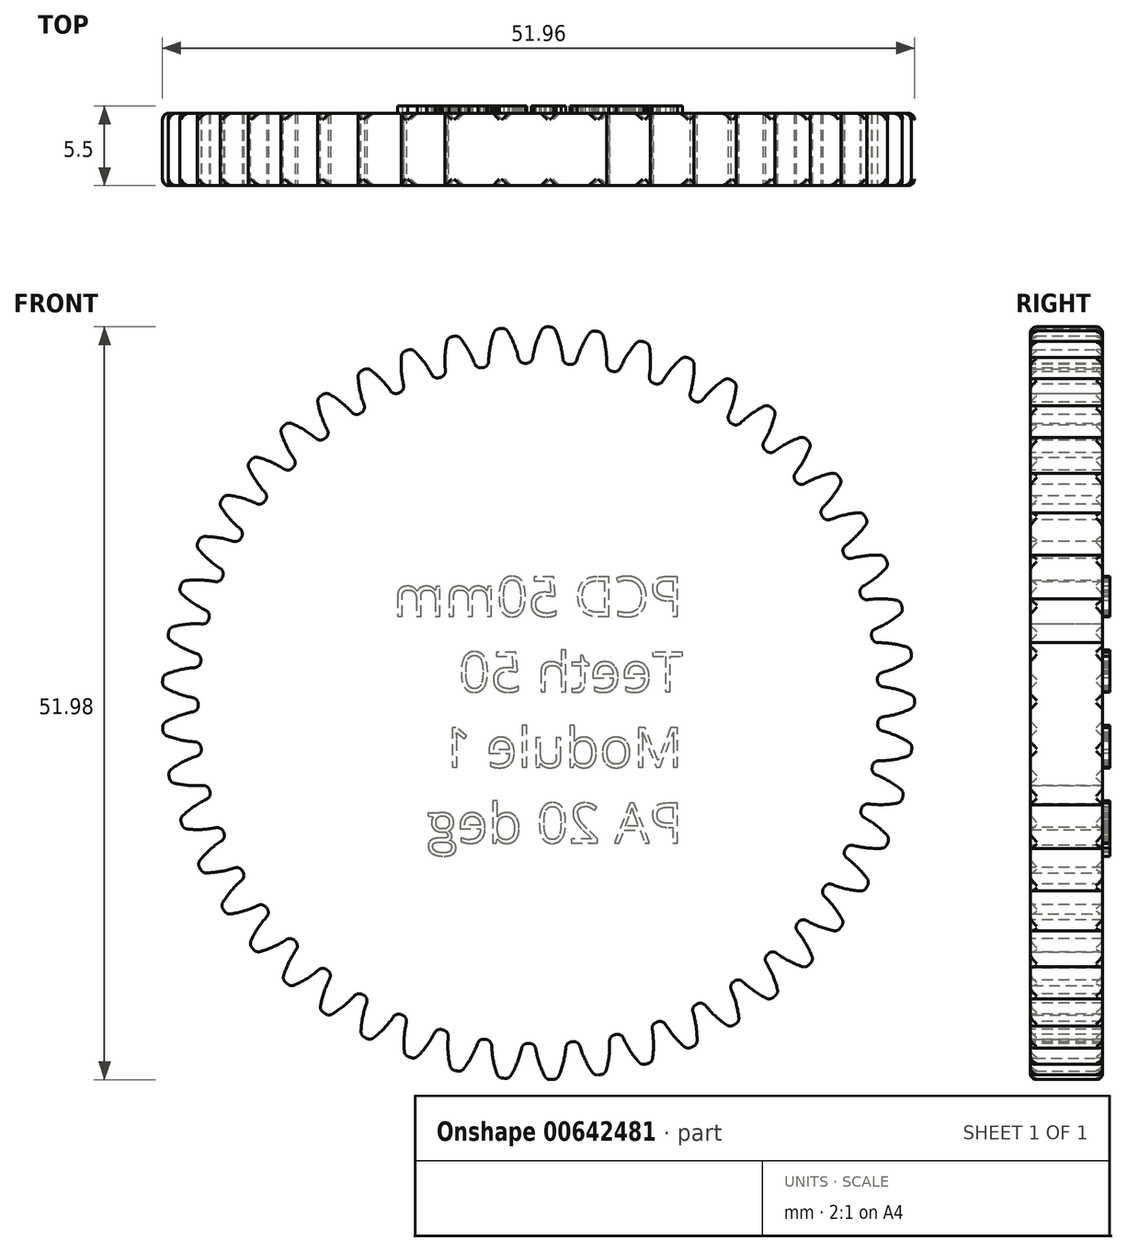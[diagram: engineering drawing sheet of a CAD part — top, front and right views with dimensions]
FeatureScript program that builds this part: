
annotation { "Feature Type Name" : "Feature", "Feature Type Description" : "" }
export const myFeature = defineFeature(function(context is Context, id is Id, definition is map)
    precondition{}
    {
        {
            var Q0;
            Q0=qCreatedBy(makeId("Front.planeOp"),FACE);
            var sketch = newSketch(context, id + "F0", { "sketchPlane" : qUnion([Q0])});
            skCircle(sketch, "E0", {"center": v(0, 0) * mm, "radius": 23.75 * mm, "construction": true});
            skCircle(sketch, "E1", {"center": v(0, 0) * mm, "radius": 25 * mm, "construction": true});
            skCircle(sketch, "E2", {"center": v(0, 0) * mm, "radius": 23.5 * mm});
            skLineSegment(sketch, "E3", {"start": v(0, 0) * mm, "end": v(0, 43.64) * mm, "construction": true});
            skLineSegment(sketch, "E4", {"start": v(0, 43.64) * mm, "end": v(0, 25) * mm});
            skLineSegment(sketch, "E5", {"start": v(0, 25) * mm, "end": v(43.73, 25) * mm, "construction": true});
            skLineSegment(sketch, "E6", {"start": v(0, 25) * mm, "end": v(41.95, 9.73) * mm, "construction": true});
            skPoint(sketch, "E7", {"position": v(0, 23.75) * mm});
            skPoint(sketch, "E8", {"position": v(0, 26) * mm});
            skPoint(sketch, "E9", {"position": v(0, 25.25) * mm});
            skLineSegment(sketch, "E10", {"start": v(0, 0) * mm, "end": v(8.03, 22.08) * mm});
            skLineSegment(sketch, "E11", {"start": v(0, 25.25) * mm, "end": v(8.03, 22.08) * mm, "construction": true});
            skPoint(sketch, "E12", {"position": v(6.03, 22.87) * mm});
            skPoint(sketch, "E13", {"position": v(-0.1, 25) * mm});
            skPoint(sketch, "E14", {"position": v(0.7, 25) * mm});
            skLineSegment(sketch, "E15", {"start": v(0.7, 25) * mm, "end": v(0, 0) * mm, "construction": true});
            skArc(sketch, "E16", {"start": v(-0.42, 23.49) * mm, "mid": v(12.22, 20.96) * mm, "end": v(0.35, 26) * mm, "construction": true});
            skArc(sketch, "E17", {"start": v(0.35, 26) * mm, "mid": v(-0.16, 24.78) * mm, "end": v(-0.42, 23.49) * mm});
            skArc(sketch, "E18", {"start": v(1.09, 25.98) * mm, "mid": v(1.54, 24.74) * mm, "end": v(1.72, 23.43) * mm});
            skArc(sketch, "E19", {"start": v(1.72, 23.43) * mm, "mid": v(-11.04, 21.6) * mm, "end": v(1.09, 25.98) * mm, "construction": true});
            skArc(sketch, "E20", {"start": v(1.09, 25.98) * mm, "mid": v(0.72, 26) * mm, "end": v(0.35, 26) * mm});
            skArc(sketch, "E21", {"start": v(0.35, 26) * mm, "mid": v(-0.72, -26) * mm, "end": v(1.09, 25.98) * mm, "construction": true});
            skSolve(sketch);
        }
        {
            var Q0;
            Q0 = qSketchRegion(id + "F0", true);
            extrude(context, id + "F1", {"entities" : qUnion([Q0]), "depth" : 5 * mm, "offsetDistance" : 25 * mm});
        }
        {
            var Q0;
            Q0=makeQuery(id+"F1.opExtrude","SWEPT_EDGE",EDGE,{"disambiguationData":[OSD([sQuery(id+"F0.wireOp",EDGE,"E2"),sQuery(id+"F0.wireOp",EDGE,"E18")])]});
            var Q1;
            Q1=makeQuery(id+"F1.opExtrude","SWEPT_EDGE",EDGE,{"disambiguationData":[OSD([sQuery(id+"F0.wireOp",EDGE,"E2"),sQuery(id+"F0.wireOp",EDGE,"E17")])]});
            var Q2;
            Q2=makeQuery(id+"F1.opExtrude","SWEPT_FACE",FACE,{"disambiguationData":[OSD([sQuery(id+"F0.wireOp",EDGE,"E20")])]});
            fillet(context, id + "F2", {"entities" : qUnion([Q0, Q1, Q2]), "radius" : 0.45 * mm, "tangentPropagation" : true, "allowEdgeOverflow" : false});
        }
        {
            var Q0;
            Q0=makeQuery(id+"F1.opExtrude","SWEPT_BODY",BODY,{"disambiguationData":[OSD([sQuery(id+"F0.wireOp",EDGE,"E2"),sQuery(id+"F0.wireOp",EDGE,"E17"),sQuery(id+"F0.wireOp",EDGE,"E18"),sQuery(id+"F0.wireOp",EDGE,"E20")])]});
            var Q1;
            Q1=makeQuery(id+"F1.opExtrude","SWEPT_FACE",FACE,{"disambiguationData":[OSD([sQuery(id+"F0.wireOp",EDGE,"E2")])]});
            circularPattern(context, id + "F3", {"operationType" : NewBodyOperationType.ADD, "entities" : qUnion([Q0]), "axis" : qUnion([Q1]), "angle" : 360 * degree, "instanceCount" : 49, "equalSpace" : true});
        }
        {
            var Q0;
            Q0=makeQuery(id+"F1.opExtrude","CAP_FACE",FACE,{"disambiguationData":[OSD([sQuery(id+"F0.wireOp",EDGE,"E2"),sQuery(id+"F0.wireOp",EDGE,"E17"),sQuery(id+"F0.wireOp",EDGE,"E18"),sQuery(id+"F0.wireOp",EDGE,"E20")])],"isStart":true});
            var sketch = newSketch(context, id + "F4", { "sketchPlane" : qUnion([Q0])});
            skText(sketch, "E22", { "text": "PCD 50mm \nTeeth 50 \nModule 1\nPA 20 deg", "fontName": "OpenSans-Regular.ttf"});
            const initialGuessF4  = {"E22": [-0.01, 0.006, 1, 0, 0.00276]};
            skSetInitialGuess(sketch, initialGuessF4);
            skSolve(sketch);
        }
        {
            var Q0;
            Q0 = qSketchRegion(id + "F4", true);
            extrude(context, id + "F5", {"entities" : qUnion([Q0]), "operationType" : NewBodyOperationType.ADD, "depth" : .5 * mm, "offsetDistance" : 25 * mm});
        }
    });
